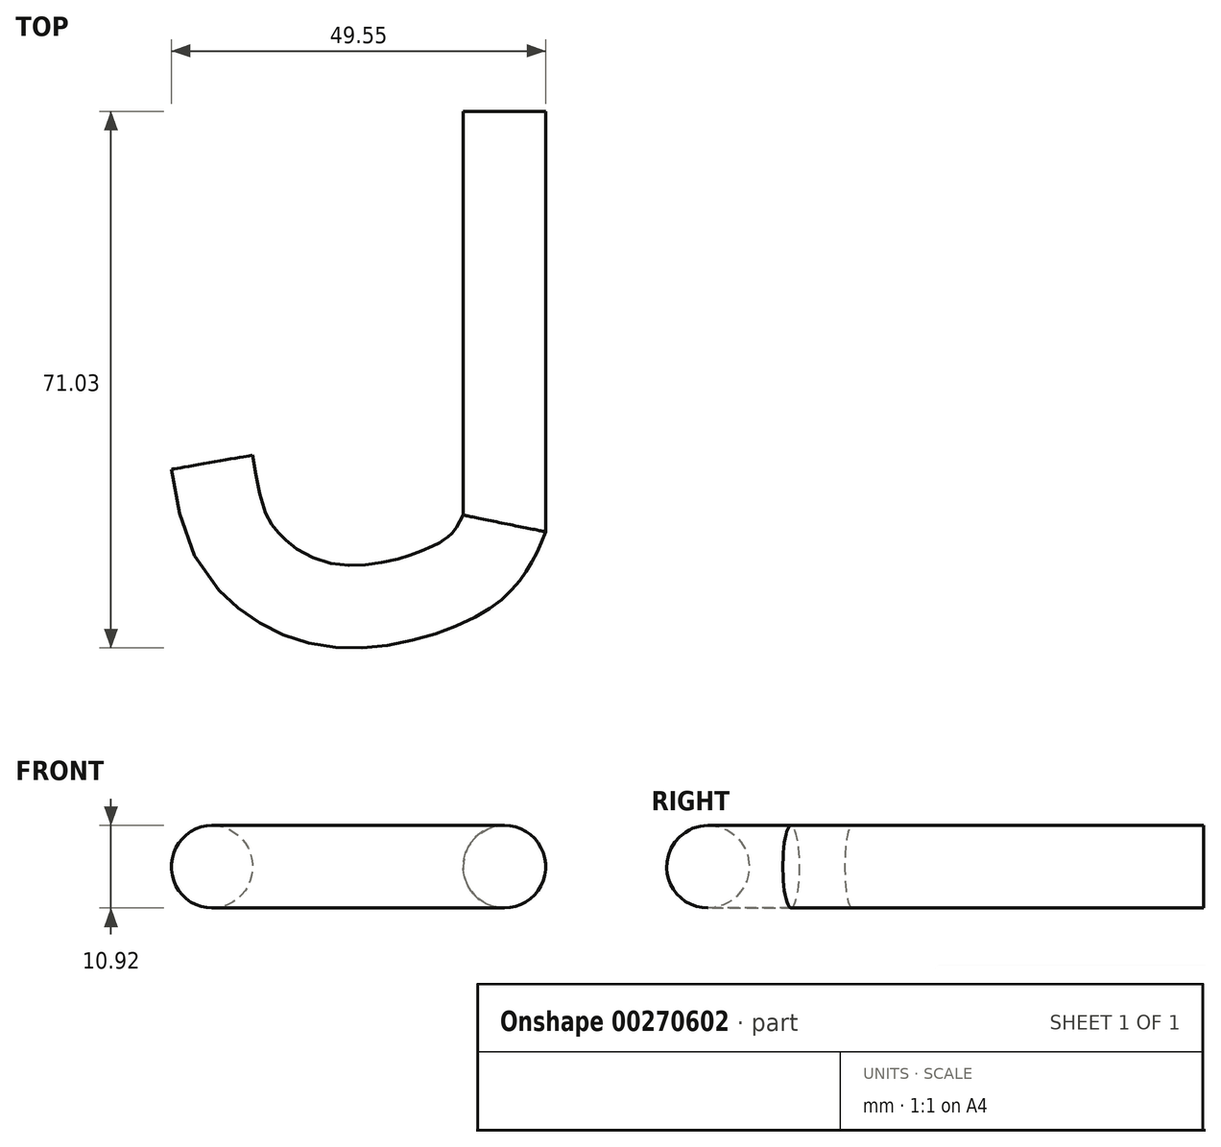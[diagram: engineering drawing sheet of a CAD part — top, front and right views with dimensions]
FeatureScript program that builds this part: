
annotation { "Feature Type Name" : "Feature", "Feature Type Description" : "" }
export const myFeature = defineFeature(function(context is Context, id is Id, definition is map)
    precondition{}
    {
        {
            var Q0;
            Q0=qCreatedBy(makeId("Front.planeOp"),FACE);
            var sketch = newSketch(context, id + "F0", { "sketchPlane" : qUnion([Q0])});
            skCircle(sketch, "E0", {"center": v(0, 0) * mm, "radius": 5.46 * mm});
            skSolve(sketch);
        }
        {
            var Q0;
            Q0=qCreatedBy(makeId("Top.planeOp"),FACE);
            var sketch = newSketch(context, id + "F1", { "sketchPlane" : qUnion([Q0])});
            skLineSegment(sketch, "E1", {"start": v(0, 0) * mm, "end": v(0, -54.57) * mm});
            skFitSpline(sketch, "E2", {"points": [v(0, -54.57) * mm, v(-6.45, -62.13) * mm, v(-23.78, -65.26) * mm, v(-35.58, -57.33) * mm, v(-38.71, -46.46) * mm], "startDerivative": vector(-22.75, -54.88) * mm, "endDerivative": vector(-10.2, 58.78) * mm});
            skSolve(sketch);
        }
        {
            var Q0;
            Q0=makeQuery(id+"F0.imprint","IMPRINT",FACE,{"disambiguationData":[TD([[makeQuery(id+"F0.imprint","IMPRINT",EDGE,{"derivedFrom":sQuery(id+"F0.wireOp",EDGE,"E0")}),1.0]])]});
            var Q1;
            Q1=sQuery(id+"F1.wireOp",EDGE,"E1");
            var Q2;
            Q2=sQuery(id+"F1.wireOp",EDGE,"E2");
            var Q3;
            Q3=sQuery(id+"F1.wireOp",EDGE,"DFIa9Lqt-hWnl-eavC-eC3p-oK9XVPhHniwy");
            sweep(context, id + "F2", {"profiles" : qUnion([Q0]), "path" : qUnion([Q1, Q2, Q3])});
        }
    });
